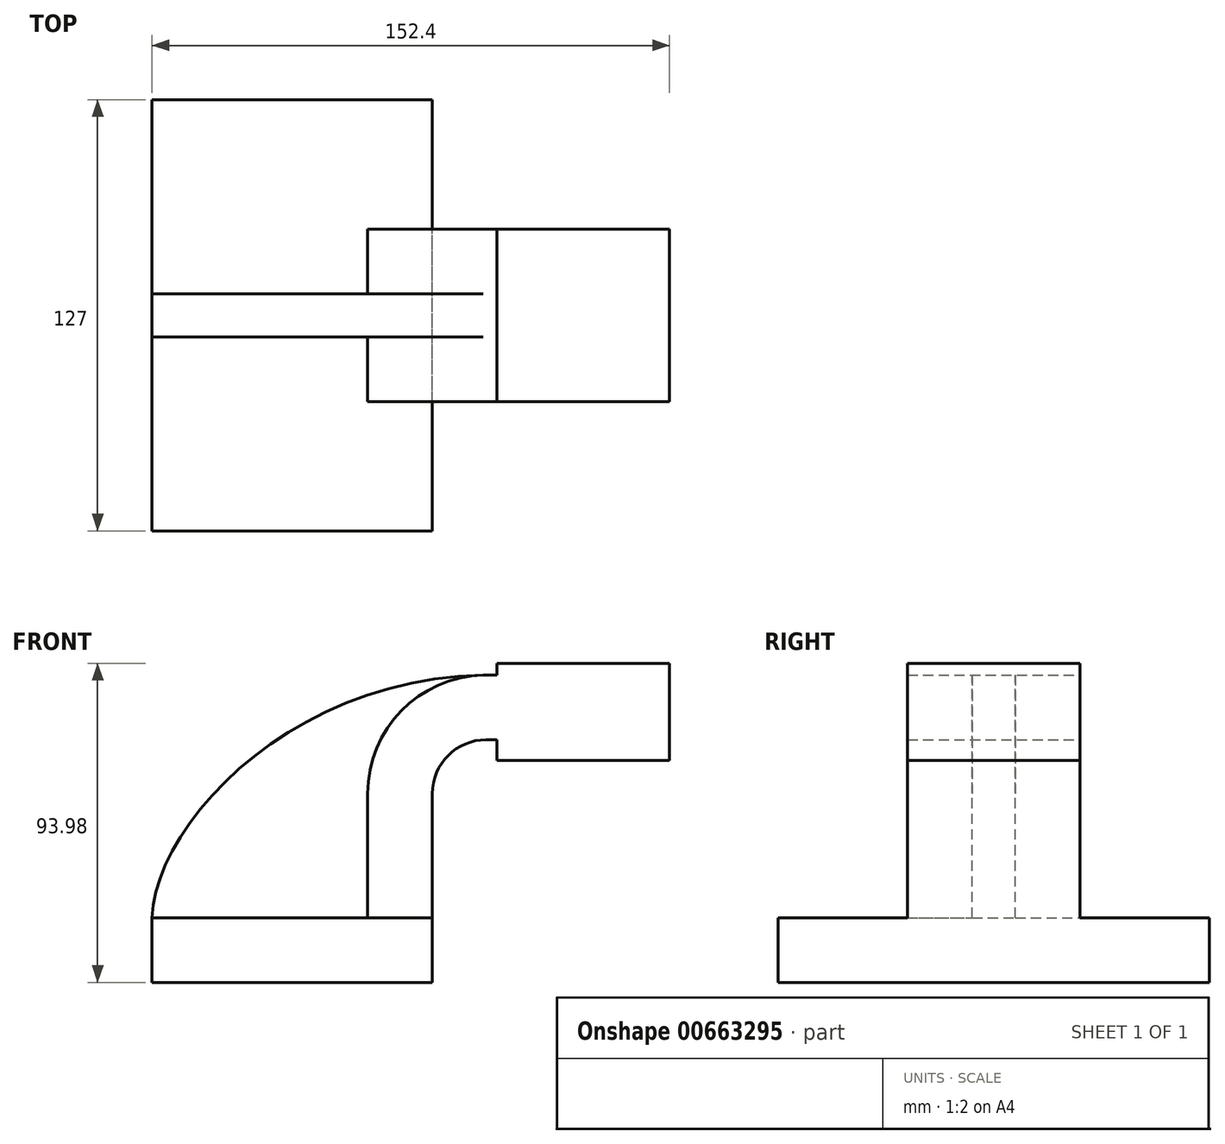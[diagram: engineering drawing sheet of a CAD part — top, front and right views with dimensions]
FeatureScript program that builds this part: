
annotation { "Feature Type Name" : "Feature", "Feature Type Description" : "" }
export const myFeature = defineFeature(function(context is Context, id is Id, definition is map)
    precondition{}
    {
        {
            var Q0;
            Q0=qCreatedBy(makeId("Front.planeOp"),FACE);
            var sketch = newSketch(context, id + "F0", { "sketchPlane" : qUnion([Q0])});
            skLineSegment(sketch, "E0.bottom", {"start": v(-41.28, 9.53) * mm, "end": v(41.28, 9.53) * mm});
            skLineSegment(sketch, "E0.top", {"start": v(-41.28, -9.52) * mm, "end": v(41.28, -9.52) * mm});
            skLineSegment(sketch, "E0.left", {"start": v(-41.28, 9.53) * mm, "end": v(-41.28, -9.52) * mm});
            skLineSegment(sketch, "E0.right", {"start": v(41.28, 9.53) * mm, "end": v(41.28, -9.52) * mm});
            skPoint(sketch, "E0.middle", {"position": v(0, 0) * mm});
            skLineSegment(sketch, "E1.bottom", {"start": v(60.33, 84.45) * mm, "end": v(111.13, 84.45) * mm});
            skLineSegment(sketch, "E1.top", {"start": v(60.33, 55.88) * mm, "end": v(111.13, 55.88) * mm});
            skLineSegment(sketch, "E1.left", {"start": v(60.33, 84.45) * mm, "end": v(60.33, 55.88) * mm});
            skLineSegment(sketch, "E1.right", {"start": v(111.13, 84.45) * mm, "end": v(111.13, 55.88) * mm});
            skPoint(sketch, "E1.middle", {"position": v(85.73, 70.17) * mm});
            skLineSegment(sketch, "E2", {"start": v(41.28, 9.52) * mm, "end": v(41.28, 46.05) * mm});
            skArc(sketch, "E3", {"start": v(41.28, 46.05) * mm, "mid": v(45.92, 57.28) * mm, "end": v(57.15, 61.93) * mm});
            skLineSegment(sketch, "E4", {"start": v(57.15, 61.93) * mm, "end": v(87.92, 61.93) * mm});
            skLineSegment(sketch, "E5.0", {"start": v(57.15, 80.98) * mm, "end": v(87.92, 80.98) * mm});
            skArc(sketch, "E5.1", {"start": v(22.23, 46.05) * mm, "mid": v(32.45, 70.75) * mm, "end": v(57.15, 80.98) * mm});
            skLineSegment(sketch, "E5.2", {"start": v(22.23, 9.52) * mm, "end": v(22.23, 46.05) * mm});
            skLineSegment(sketch, "E6", {"start": v(87.92, 61.93) * mm, "end": v(87.92, 80.98) * mm});
            skFitSpline(sketch, "E7", {"points": [v(-41.28, 9.53) * mm, v(57.15, 80.98) * mm], "startDerivative": vector(2.97, 83.57) * mm, "endDerivative": vector(171.45, 1.55) * mm});
            skSolve(sketch);
        }
        {
            var Q0;
            Q0=makeQuery(id+"F0.imprint","IMPRINT",FACE,{"disambiguationData":[TD([[makeQuery(id+"F0.imprint","IMPRINT",EDGE,{"derivedFrom":sQuery(id+"F0.wireOp",EDGE,"E0.top")}),1.0]])]});
            extrude(context, id + "F1", {"entities" : qUnion([Q0]), "endBound" : BoundingType.SYMMETRIC, "depth" : 127 * mm, "offsetDistance" : 25.4 * mm});
        }
        {
            var Q0;
            {var subQ1=sQuery(id+"F0.wireOp",EDGE,"E2");Q0=makeQuery(id+"F0.imprint","IMPRINT",FACE,{"disambiguationData":[TD([[makeQuery(id+"F0.imprint","IMPRINT",EDGE,{"derivedFrom":subQ1}),1.0]])]});}
            var Q1;
            {var subQ5=sQuery(id+"F0.wireOp",EDGE,"E6");Q1=makeQuery(id+"F0.imprint","IMPRINT",FACE,{"disambiguationData":[TD([[makeQuery(id+"F0.imprint","IMPRINT",EDGE,{"derivedFrom":subQ5}),1.0]])]});}
            var Q2;
            {var subQ5=sQuery(id+"F0.wireOp",EDGE,"E1.bottom");Q2=makeQuery(id+"F0.imprint","IMPRINT",FACE,{"disambiguationData":[TD([[makeQuery(id+"F0.imprint","IMPRINT",EDGE,{"derivedFrom":subQ5}),-1.0]])]});}
            extrude(context, id + "F2", {"entities" : qUnion([Q0, Q1, Q2]), "operationType" : NewBodyOperationType.ADD, "endBound" : BoundingType.SYMMETRIC, "depth" : 50.8 * mm, "offsetDistance" : 25.4 * mm});
        }
        {
            var Q0;
            {var subQ3=sQuery(id+"F0.wireOp",EDGE,"E5.2");Q0=makeQuery(id+"F0.imprint","IMPRINT",FACE,{"disambiguationData":[TD([[makeQuery(id+"F0.imprint","IMPRINT",EDGE,{"derivedFrom":subQ3}),1.0]])]});}
            extrude(context, id + "F3", {"entities" : qUnion([Q0]), "operationType" : NewBodyOperationType.ADD, "endBound" : BoundingType.SYMMETRIC, "depth" : 12.7 * mm, "offsetDistance" : 25.4 * mm});
        }
    });
